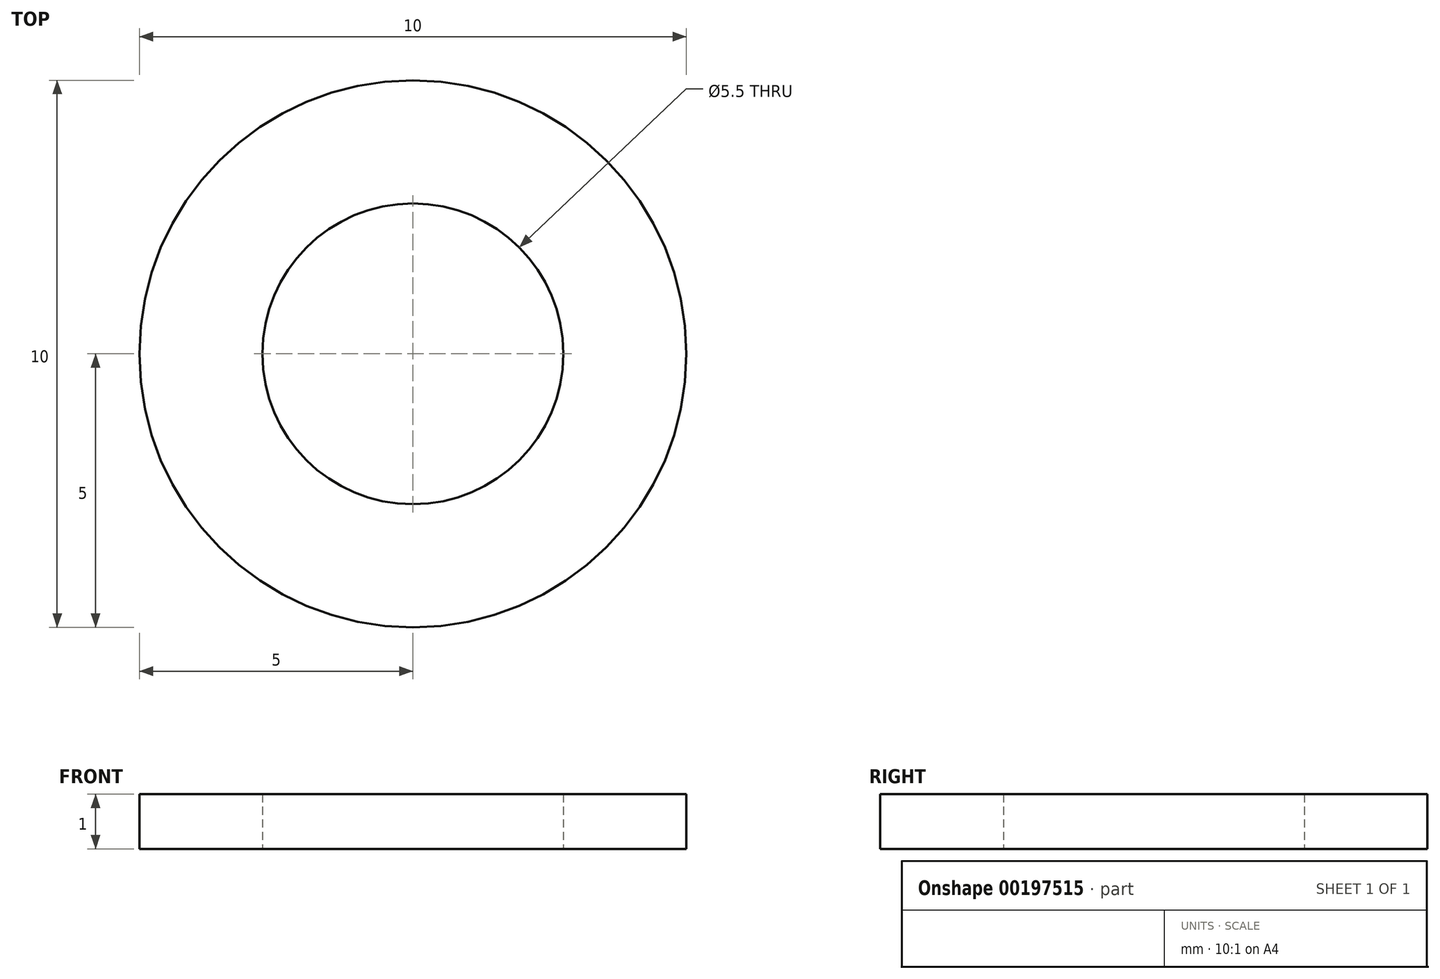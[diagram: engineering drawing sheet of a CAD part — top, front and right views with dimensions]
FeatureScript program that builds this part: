
annotation { "Feature Type Name" : "Feature", "Feature Type Description" : "" }
export const myFeature = defineFeature(function(context is Context, id is Id, definition is map)
    precondition{}
    {
        {
            var Q0;
            Q0=qCreatedBy(makeId("Top.planeOp"),FACE);
            var sketch = newSketch(context, id + "F0", { "sketchPlane" : qUnion([Q0])});
            skCircle(sketch, "E0", {"center": v(0, 0) * mm, "radius": 2.75 * mm});
            skCircle(sketch, "E1", {"center": v(0, 0) * mm, "radius": 5 * mm});
            skSolve(sketch);
        }
        {
            var Q0;
            Q0=qSketchRegion(id+"F0",true);
            extrude(context, id + "F1", {"entities" : qUnion([Q0]), "depth" : 1 * mm});
        }
    });
